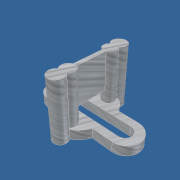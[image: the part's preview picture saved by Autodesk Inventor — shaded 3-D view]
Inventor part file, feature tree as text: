
AUTODESK INVENTOR PART (.ipt)
format: ipt  version: unknown  size: 224,256 bytes
history: native  units: mm
features: extrude x3, sketch x3
ambient origin geometry x8: Origin, YZ Plane, XZ Plane, XY Plane, X Axis, Y Axis, Z Axis, Center Point
feature tree (6):
  extrude  "Выдавливание1"  Depth=6.0mm
  extrude  "Выдавливание2"  Depth=21.0mm
  extrude  "Выдавливание3"  Depth=5.85mm
  sketch  "Эскиз1"
  sketch  "Эскиз2"
  sketch  "Эскиз3"
